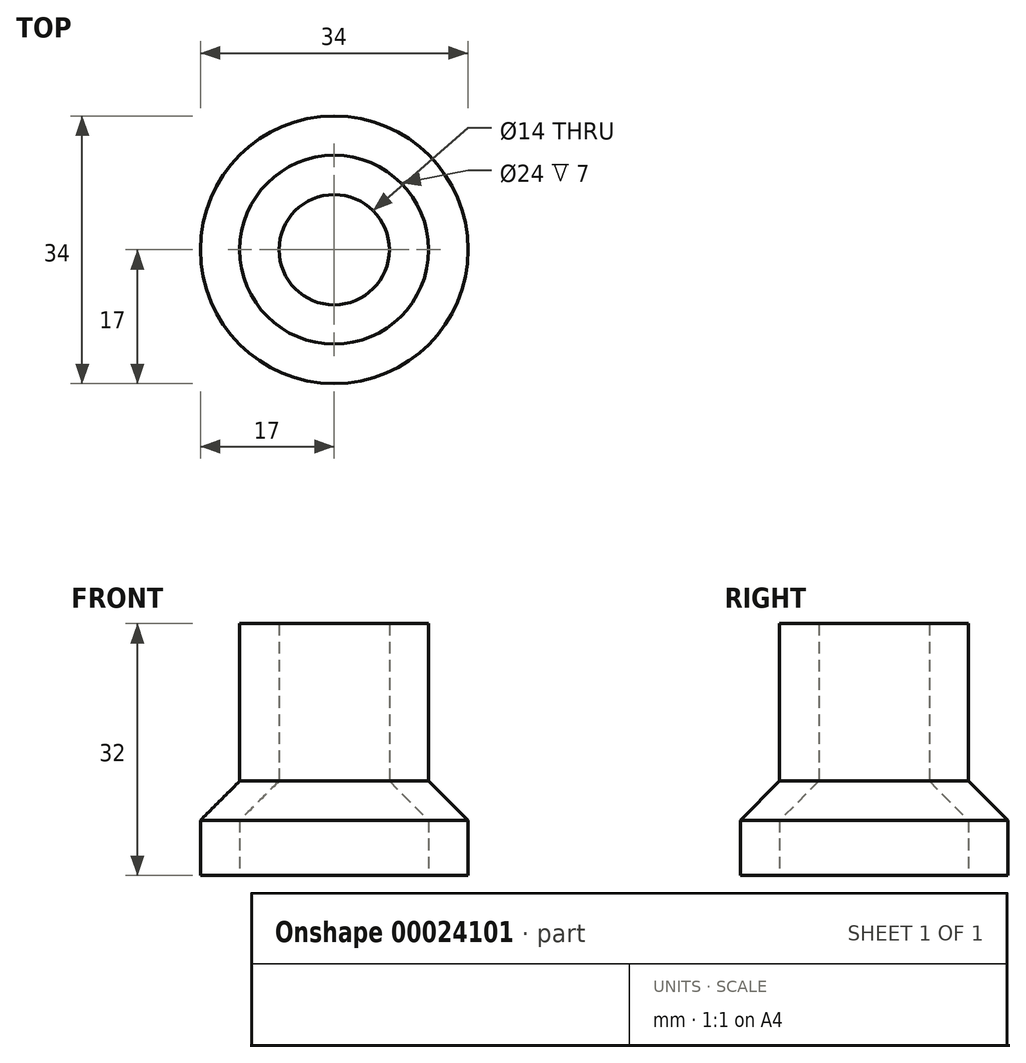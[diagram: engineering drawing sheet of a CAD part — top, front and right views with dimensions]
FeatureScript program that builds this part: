
annotation { "Feature Type Name" : "Feature", "Feature Type Description" : "" }
export const myFeature = defineFeature(function(context is Context, id is Id, definition is map)
    precondition{}
    {
        {
            var Q0;
            Q0=qCreatedBy(makeId("Right.planeOp"),FACE);
            var sketch = newSketch(context, id + "F0", { "sketchPlane" : qUnion([Q0])});
            skLineSegment(sketch, "E0", {"start": v(12, 0) * mm, "end": v(17, 0) * mm});
            skLineSegment(sketch, "E1", {"start": v(17, 0) * mm, "end": v(17, 7) * mm});
            skLineSegment(sketch, "E2", {"start": v(12, 0) * mm, "end": v(12, 7) * mm});
            skLineSegment(sketch, "E3", {"start": v(12, 7) * mm, "end": v(7, 12) * mm});
            skLineSegment(sketch, "E4", {"start": v(7, 12) * mm, "end": v(7, 32) * mm});
            skLineSegment(sketch, "E5", {"start": v(7, 32) * mm, "end": v(12, 32) * mm});
            skLineSegment(sketch, "E6", {"start": v(12, 32) * mm, "end": v(12, 12) * mm});
            skLineSegment(sketch, "E7", {"start": v(12, 12) * mm, "end": v(17, 7) * mm});
            skLineSegment(sketch, "E8", {"start": v(0, 0) * mm, "end": v(0, 75.99) * mm});
            skLineSegment(sketch, "E9", {"start": v(0, 0) * mm, "end": v(12, 0) * mm});
            skLineSegment(sketch, "E10", {"start": v(7, 32) * mm, "end": v(0, 32) * mm});
            skSolve(sketch);
        }
        {
            var Q0;
            Q0=makeQuery(id+"F0.imprint","IMPRINT",FACE,{"disambiguationData":[TD([[makeQuery(id+"F0.imprint","IMPRINT",EDGE,{"derivedFrom":sQuery(id+"F0.wireOp",EDGE,"E0")}),1.0]])]});
            var Q1;
            Q1=sQuery(id+"F0.wireOp",EDGE,"E8");
            revolve(context, id + "F1", {"entities" : qUnion([Q0]), "axis" : qUnion([Q1]), "revolveType" : RevolveType.FULL});
        }
    });
